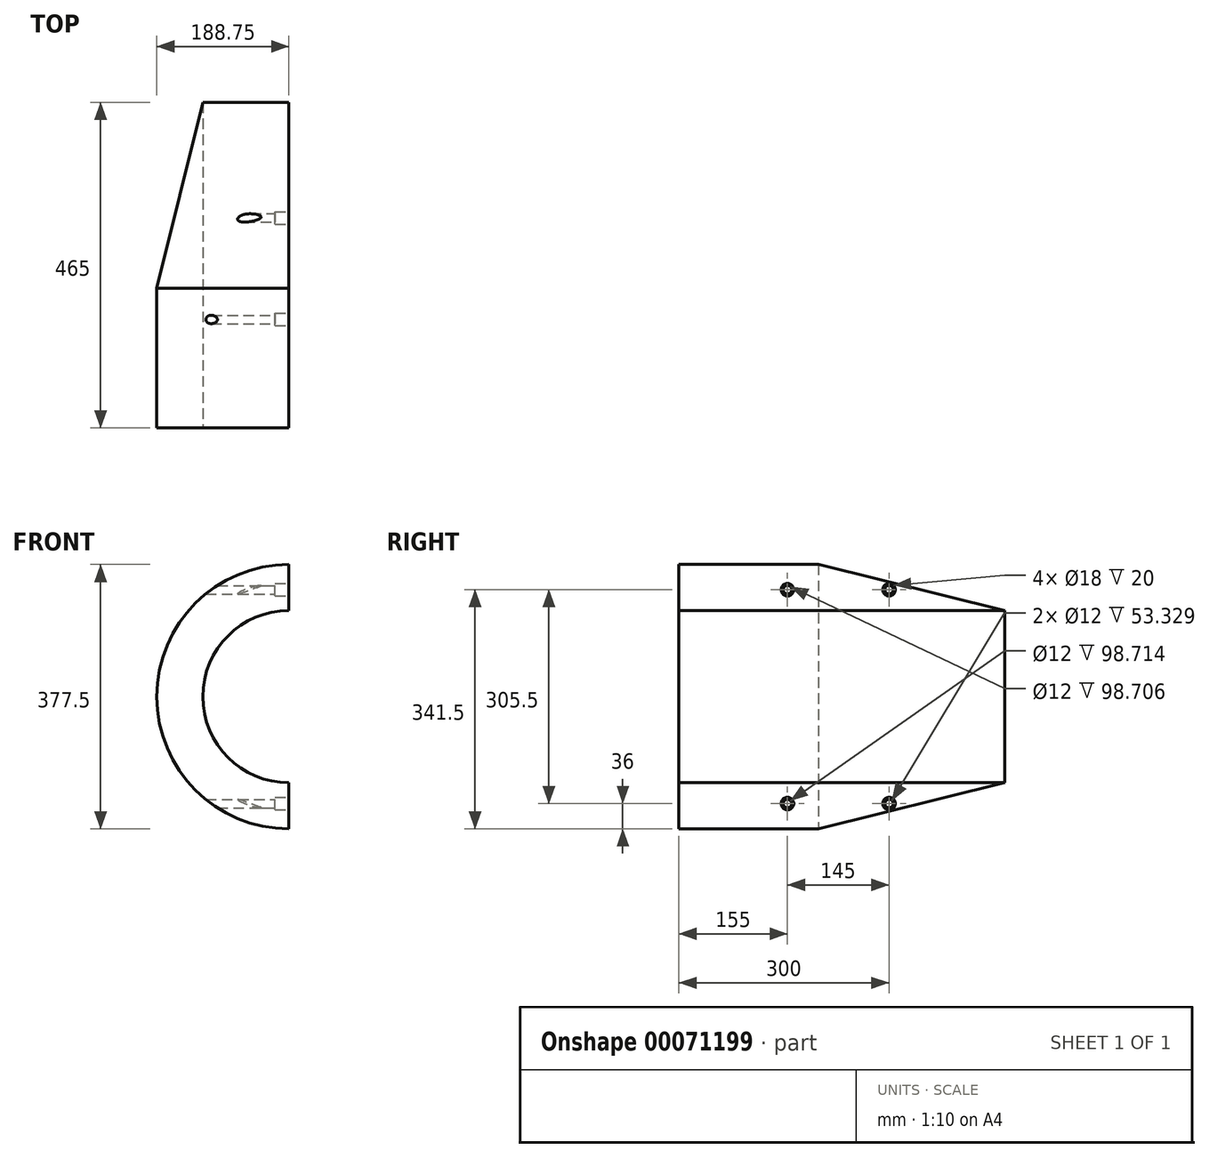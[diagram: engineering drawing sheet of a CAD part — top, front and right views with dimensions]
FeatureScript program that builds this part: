
annotation { "Feature Type Name" : "Feature", "Feature Type Description" : "" }
export const myFeature = defineFeature(function(context is Context, id is Id, definition is map)
    precondition{}
    {
        {
            var Q0;
            Q0=qCreatedBy(makeId("Top.planeOp"),FACE);
            var sketch = newSketch(context, id + "F0", { "sketchPlane" : qUnion([Q0])});
            skLineSegment(sketch, "E0", {"start": v(-123, 0) * mm, "end": v(-188.75, 0) * mm});
            skLineSegment(sketch, "E1", {"start": v(-188.75, 0) * mm, "end": v(-188.75, 199.4) * mm});
            skLineSegment(sketch, "E2", {"start": v(-188.75, 199.4) * mm, "end": v(-123, 465) * mm});
            skLineSegment(sketch, "E3", {"start": v(-123, 465) * mm, "end": v(-123, 0) * mm});
            skSolve(sketch);
        }
        {
            var Q0;
            Q0=qCreatedBy(makeId("Top.planeOp"),FACE);
            var sketch = newSketch(context, id + "F1", { "sketchPlane" : qUnion([Q0])});
            skLineSegment(sketch, "E4", {"start": v(0, 0) * mm, "end": v(0, 140.88) * mm});
            skSolve(sketch);
        }
        {
            var Q0;
            Q0 = qSketchRegion(id + "F0", true);
            var Q1;
            Q1=sQuery(id+"F1.wireOp",EDGE,"E4");
            revolve(context, id + "F2", {"entities" : qUnion([Q0]), "axis" : qUnion([Q1]), "revolveType" : RevolveType.SYMMETRIC, "angle" : 180 * degree});
        }
        {
            var Q0;
            Q0=makeQuery(id+"F2.opRevolve","CAP_FACE",FACE,{"disambiguationData":[OSD([sQuery(id+"F0.wireOp",EDGE,"E0"),sQuery(id+"F0.wireOp",EDGE,"E1"),sQuery(id+"F0.wireOp",EDGE,"E2"),sQuery(id+"F0.wireOp",EDGE,"E3")])],"isStart":false});
            var sketch = newSketch(context, id + "F3", { "sketchPlane" : qUnion([Q0])});
            skPoint(sketch, "E5", {"position": v(155, 152.75) * mm});
            skPoint(sketch, "E6", {"position": v(300, 152.75) * mm});
            skPoint(sketch, "E7", {"position": v(155, -152.75) * mm});
            skPoint(sketch, "E8", {"position": v(300, -152.75) * mm});
            skSolve(sketch);
        }
        {
            var Q0;
            Q0=sQuery(id+"F3.wireOp",VERTEX,"E5");
            var Q1;
            Q1=sQuery(id+"F3.wireOp",VERTEX,"E6");
            var Q2;
            Q2=sQuery(id+"F3.wireOp",VERTEX,"E8");
            var Q3;
            Q3=sQuery(id+"F3.wireOp",VERTEX,"E7");
            var Q4;
            Q4=makeQuery(id+"F2.opRevolve","SWEPT_BODY",BODY,{"disambiguationData":[OSD([sQuery(id+"F0.wireOp",EDGE,"E0"),sQuery(id+"F0.wireOp",EDGE,"E1"),sQuery(id+"F0.wireOp",EDGE,"E2"),sQuery(id+"F0.wireOp",EDGE,"E3")])]});
            hole(context, id + "F4", {"style" : HoleStyle.C_BORE, "holeDiameter" : 12 * mm, "cBoreDiameter" : 18 * mm, "cBoreDepth" : 20 * mm, "endStyle" : HoleEndStyle.THROUGH, "locations" : qUnion([Q0, Q1, Q2, Q3]), "scope" : qUnion([Q4])});
        }
    });
